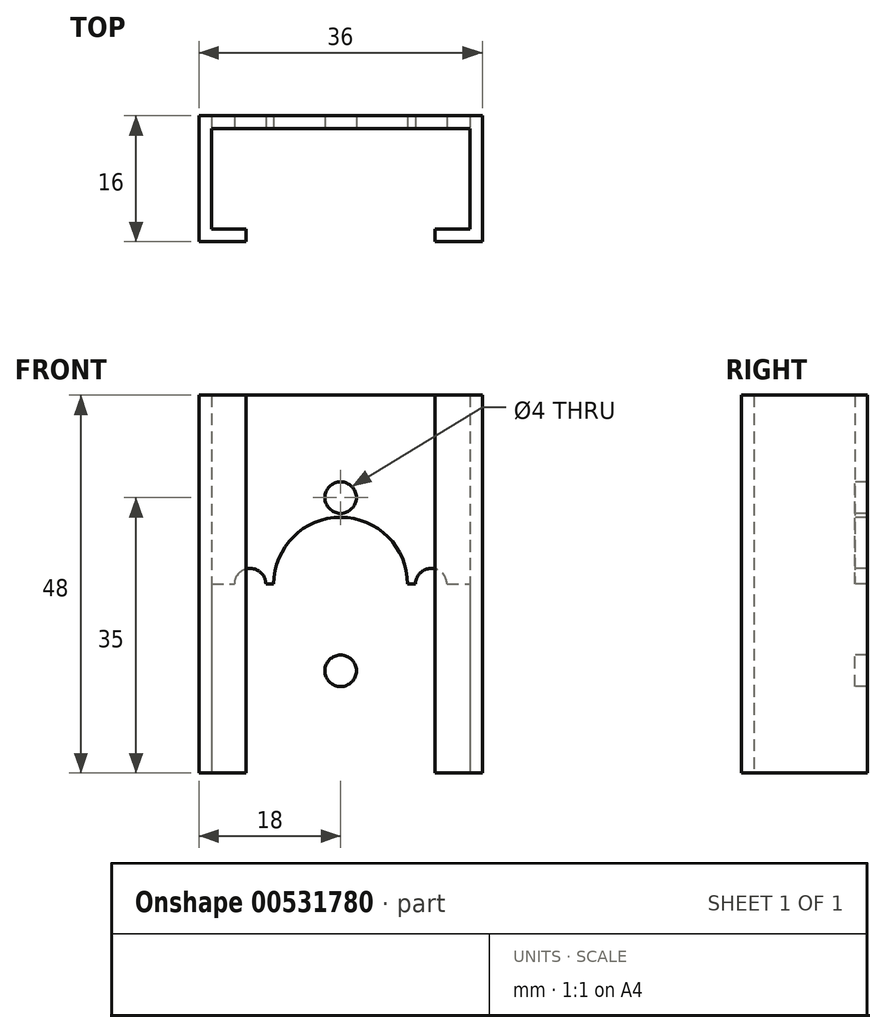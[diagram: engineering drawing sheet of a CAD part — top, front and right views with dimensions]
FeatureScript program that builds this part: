
annotation { "Feature Type Name" : "Feature", "Feature Type Description" : "" }
export const myFeature = defineFeature(function(context is Context, id is Id, definition is map)
    precondition{}
    {
        {
            var Q0;
            Q0=qCreatedBy(makeId("Top.planeOp"),FACE);
            var sketch = newSketch(context, id + "F0", { "sketchPlane" : qUnion([Q0])});
            skLineSegment(sketch, "E0.bottom", {"start": v(18, -8) * mm, "end": v(-18, -8) * mm});
            skLineSegment(sketch, "E0.top", {"start": v(18, 8) * mm, "end": v(-18, 8) * mm});
            skLineSegment(sketch, "E0.left", {"start": v(18, -8) * mm, "end": v(18, 8) * mm});
            skLineSegment(sketch, "E0.right", {"start": v(-18, -8) * mm, "end": v(-18, 8) * mm});
            skPoint(sketch, "E0.middle", {"position": v(0, 0) * mm});
            skLineSegment(sketch, "E1", {"start": v(-12, -8) * mm, "end": v(-12, -6.4) * mm});
            skLineSegment(sketch, "E2", {"start": v(-12, -6.4) * mm, "end": v(-16.4, -6.4) * mm});
            skLineSegment(sketch, "E3", {"start": v(-16.4, -6.4) * mm, "end": v(-16.4, 6.4) * mm});
            skLineSegment(sketch, "E4", {"start": v(-16.4, 6.4) * mm, "end": v(16.4, 6.4) * mm});
            skLineSegment(sketch, "E5", {"start": v(16.4, 6.4) * mm, "end": v(16.4, -6.4) * mm});
            skLineSegment(sketch, "E6", {"start": v(16.4, -6.4) * mm, "end": v(12, -6.4) * mm});
            skLineSegment(sketch, "E7", {"start": v(12, -6.4) * mm, "end": v(12, -8) * mm});
            skSolve(sketch);
        }
        {
            var Q0;
            Q0=makeQuery(id+"F0.imprint","IMPRINT",FACE,{"disambiguationData":[TD([[makeQuery(id+"F0.imprint","IMPRINT",EDGE,{"derivedFrom":sQuery(id+"F0.wireOp",EDGE,"E0.top")}),1.0]])]});
            extrude(context, id + "F1", {"entities" : qUnion([Q0]), "depth" : 48 * mm, "offsetDistance" : 25 * mm});
        }
        {
            var Q0;
            Q0=makeQuery(id+"F1.opExtrude","SWEPT_FACE",FACE,{"disambiguationData":[OSD([sQuery(id+"F0.wireOp",EDGE,"E4")])]});
            var sketch = newSketch(context, id + "F2", { "sketchPlane" : qUnion([Q0])});
            skLineSegment(sketch, "E8", {"start": v(0, 48) * mm, "end": v(0, 0) * mm});
            skLineSegment(sketch, "E9", {"start": v(-16.4, 24) * mm, "end": v(0, 24) * mm});
            skLineSegment(sketch, "E10", {"start": v(0, 24) * mm, "end": v(16.4, 24) * mm});
            skCircle(sketch, "E11", {"center": v(0, 24) * mm, "radius": 8.5 * mm});
            skCircle(sketch, "E12", {"center": v(0, 35) * mm, "radius": 2 * mm});
            skCircle(sketch, "E13", {"center": v(0, 13) * mm, "radius": 2 * mm});
            skCircle(sketch, "E14", {"center": v(11.5, 24) * mm, "radius": 2 * mm});
            skCircle(sketch, "E15", {"center": v(-11.5, 24) * mm, "radius": 2 * mm});
            skSolve(sketch);
        }
        {
            var Q0;
            {var subQ1=sQuery(id+"F2.wireOp",EDGE,"E8");var subQ3=sQuery(id+"F2.wireOp",EDGE,"E11");var subQ4=makeQuery(id+"F2.imprint","INTERSECT",VERTEX,{"disambiguationData":[OD(0.0)],"derivedFrom":[subQ1,subQ3]});Q0=makeQuery(id+"F2.imprint","IMPRINT",FACE,{"disambiguationData":[TD([[makeQuery(id+"F2.imprint","IMPRINT",EDGE,{"disambiguationData":[TD([[subQ4,-1.0]])],"derivedFrom":subQ3}),1.0]])]});}
            var Q1;
            {var subQ1=sQuery(id+"F2.wireOp",EDGE,"E8");var subQ3=sQuery(id+"F2.wireOp",EDGE,"E11");var subQ4=makeQuery(id+"F2.imprint","INTERSECT",VERTEX,{"disambiguationData":[OD(0.0)],"derivedFrom":[subQ1,subQ3]});Q1=makeQuery(id+"F2.imprint","IMPRINT",FACE,{"disambiguationData":[TD([[makeQuery(id+"F2.imprint","IMPRINT",EDGE,{"disambiguationData":[TD([[subQ4,1.0]])],"derivedFrom":subQ3}),1.0]])]});}
            var Q2;
            {var subQ1=sQuery(id+"F2.wireOp",EDGE,"E8");var subQ3=sQuery(id+"F2.wireOp",EDGE,"E11");var subQ4=makeQuery(id+"F2.imprint","INTERSECT",VERTEX,{"disambiguationData":[OD(1.0)],"derivedFrom":[subQ1,subQ3]});Q2=makeQuery(id+"F2.imprint","IMPRINT",FACE,{"disambiguationData":[TD([[makeQuery(id+"F2.imprint","IMPRINT",EDGE,{"disambiguationData":[TD([[subQ4,1.0]])],"derivedFrom":subQ3}),1.0]])]});}
            var Q3;
            {var subQ1=sQuery(id+"F2.wireOp",EDGE,"E8");var subQ3=sQuery(id+"F2.wireOp",EDGE,"E11");var subQ4=makeQuery(id+"F2.imprint","INTERSECT",VERTEX,{"disambiguationData":[OD(1.0)],"derivedFrom":[subQ1,subQ3]});Q3=makeQuery(id+"F2.imprint","IMPRINT",FACE,{"disambiguationData":[TD([[makeQuery(id+"F2.imprint","IMPRINT",EDGE,{"disambiguationData":[TD([[subQ4,-1.0]])],"derivedFrom":subQ3}),1.0]])]});}
            extrude(context, id + "F3", {"entities" : qUnion([Q0, Q1, Q2, Q3]), "operationType" : NewBodyOperationType.REMOVE, "oppositeDirection" : true, "depth" : 25 * mm, "offsetDistance" : 25 * mm});
        }
        {
            var Q0;
            {var subQ0=sQuery(id+"F2.wireOp",EDGE,"E13");var subQ1=sQuery(id+"F2.wireOp",EDGE,"E8");var subQ2=makeQuery(id+"F2.imprint","INTERSECT",VERTEX,{"disambiguationData":[OD(0.0)],"derivedFrom":[subQ1,subQ0]});Q0=makeQuery(id+"F2.imprint","IMPRINT",FACE,{"disambiguationData":[TD([[makeQuery(id+"F2.imprint","IMPRINT",EDGE,{"disambiguationData":[TD([[subQ2,-1.0]])],"derivedFrom":subQ1}),1.0]])]});}
            var Q1;
            {var subQ0=sQuery(id+"F2.wireOp",EDGE,"E13");var subQ1=sQuery(id+"F2.wireOp",EDGE,"E8");var subQ2=makeQuery(id+"F2.imprint","INTERSECT",VERTEX,{"disambiguationData":[OD(0.0)],"derivedFrom":[subQ1,subQ0]});Q1=makeQuery(id+"F2.imprint","IMPRINT",FACE,{"disambiguationData":[TD([[makeQuery(id+"F2.imprint","IMPRINT",EDGE,{"disambiguationData":[TD([[subQ2,-1.0]])],"derivedFrom":subQ1}),-1.0]])]});}
            var Q2;
            {var subQ0=sQuery(id+"F2.wireOp",EDGE,"E12");var subQ1=sQuery(id+"F2.wireOp",EDGE,"E8");var subQ2=makeQuery(id+"F2.imprint","INTERSECT",VERTEX,{"disambiguationData":[OD(0.0)],"derivedFrom":[subQ1,subQ0]});Q2=makeQuery(id+"F2.imprint","IMPRINT",FACE,{"disambiguationData":[TD([[makeQuery(id+"F2.imprint","IMPRINT",EDGE,{"disambiguationData":[TD([[subQ2,-1.0]])],"derivedFrom":subQ1}),-1.0]])]});}
            var Q3;
            {var subQ0=sQuery(id+"F2.wireOp",EDGE,"E12");var subQ1=sQuery(id+"F2.wireOp",EDGE,"E8");var subQ2=makeQuery(id+"F2.imprint","INTERSECT",VERTEX,{"disambiguationData":[OD(0.0)],"derivedFrom":[subQ1,subQ0]});Q3=makeQuery(id+"F2.imprint","IMPRINT",FACE,{"disambiguationData":[TD([[makeQuery(id+"F2.imprint","IMPRINT",EDGE,{"disambiguationData":[TD([[subQ2,-1.0]])],"derivedFrom":subQ1}),1.0]])]});}
            extrude(context, id + "F4", {"entities" : qUnion([Q0, Q1, Q2, Q3]), "operationType" : NewBodyOperationType.REMOVE, "oppositeDirection" : true, "depth" : 25 * mm, "offsetDistance" : 25 * mm});
        }
        {
            var Q0;
            {var subQ0=sQuery(id+"F2.wireOp",EDGE,"E15");var subQ1=sQuery(id+"F2.wireOp",EDGE,"E9");var subQ2=makeQuery(id+"F2.imprint","INTERSECT",VERTEX,{"disambiguationData":[OD(0.0)],"derivedFrom":[subQ1,subQ0]});Q0=makeQuery(id+"F2.imprint","IMPRINT",FACE,{"disambiguationData":[TD([[makeQuery(id+"F2.imprint","IMPRINT",EDGE,{"disambiguationData":[TD([[subQ2,-1.0]])],"derivedFrom":subQ1}),-1.0]])]});}
            var Q1;
            {var subQ0=sQuery(id+"F2.wireOp",EDGE,"E15");var subQ1=sQuery(id+"F2.wireOp",EDGE,"E9");var subQ2=makeQuery(id+"F2.imprint","INTERSECT",VERTEX,{"disambiguationData":[OD(0.0)],"derivedFrom":[subQ1,subQ0]});Q1=makeQuery(id+"F2.imprint","IMPRINT",FACE,{"disambiguationData":[TD([[makeQuery(id+"F2.imprint","IMPRINT",EDGE,{"disambiguationData":[TD([[subQ2,-1.0]])],"derivedFrom":subQ1}),1.0]])]});}
            var Q2;
            {var subQ0=sQuery(id+"F2.wireOp",EDGE,"E14");var subQ1=sQuery(id+"F2.wireOp",EDGE,"E10");var subQ2=makeQuery(id+"F2.imprint","INTERSECT",VERTEX,{"disambiguationData":[OD(0.0)],"derivedFrom":[subQ1,subQ0]});Q2=makeQuery(id+"F2.imprint","IMPRINT",FACE,{"disambiguationData":[TD([[makeQuery(id+"F2.imprint","IMPRINT",EDGE,{"disambiguationData":[TD([[subQ2,-1.0]])],"derivedFrom":subQ1}),1.0]])]});}
            var Q3;
            {var subQ0=sQuery(id+"F2.wireOp",EDGE,"E14");var subQ1=sQuery(id+"F2.wireOp",EDGE,"E10");var subQ2=makeQuery(id+"F2.imprint","INTERSECT",VERTEX,{"disambiguationData":[OD(0.0)],"derivedFrom":[subQ1,subQ0]});Q3=makeQuery(id+"F2.imprint","IMPRINT",FACE,{"disambiguationData":[TD([[makeQuery(id+"F2.imprint","IMPRINT",EDGE,{"disambiguationData":[TD([[subQ2,-1.0]])],"derivedFrom":subQ1}),-1.0]])]});}
            extrude(context, id + "F5", {"entities" : qUnion([Q0, Q1, Q2, Q3]), "operationType" : NewBodyOperationType.REMOVE, "oppositeDirection" : true, "depth" : 25 * mm, "offsetDistance" : 25 * mm});
        }
    });
